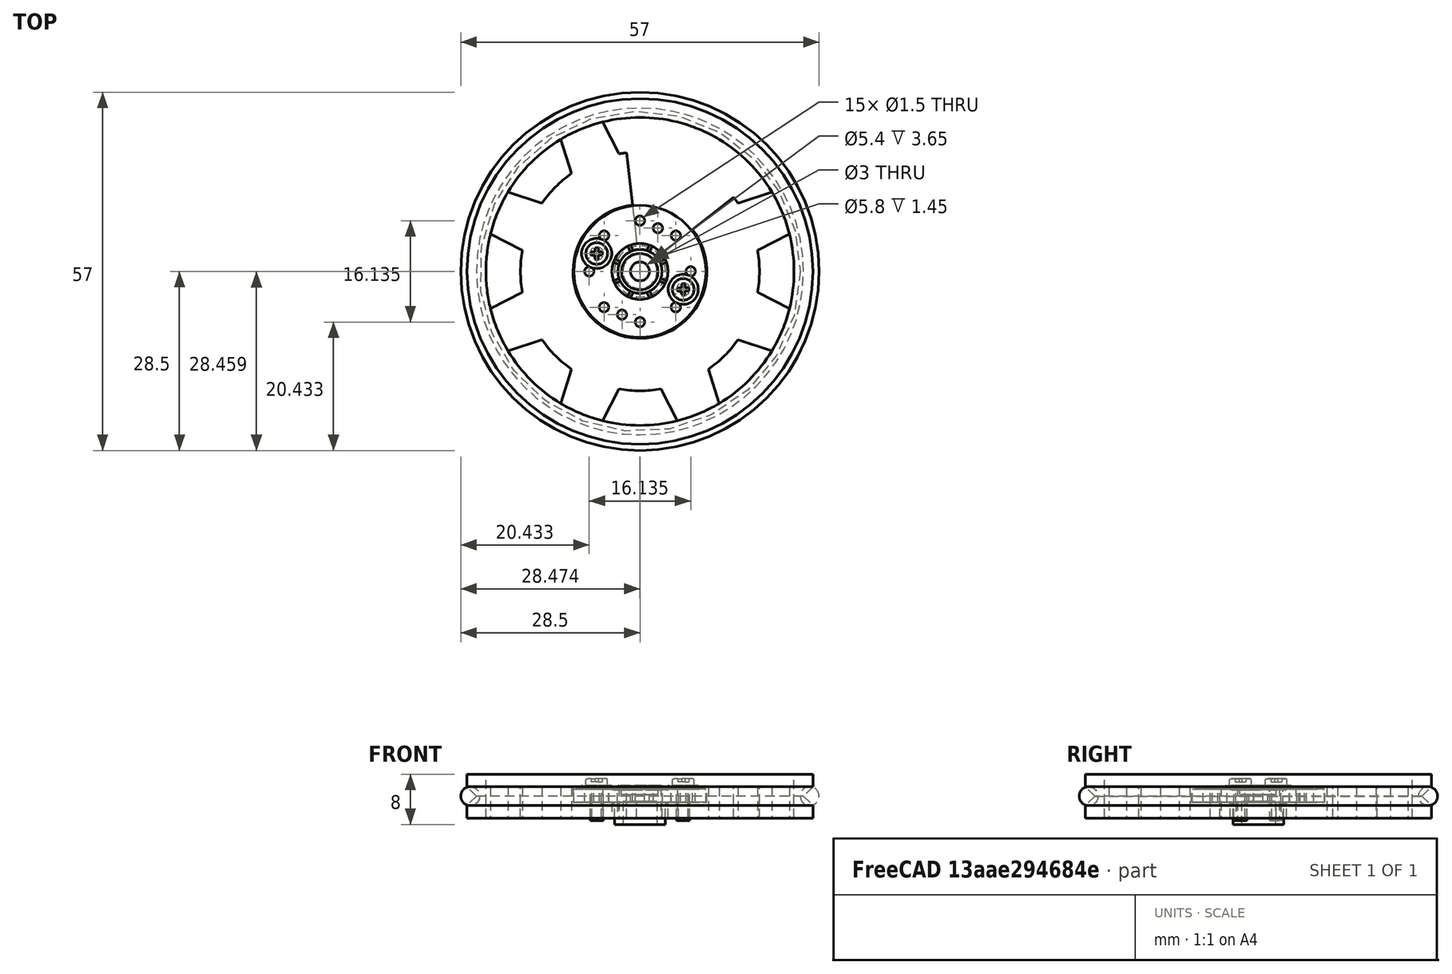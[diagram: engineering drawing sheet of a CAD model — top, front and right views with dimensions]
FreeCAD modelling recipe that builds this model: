
FCSTD DOCUMENT  (FreeCAD 0.14R3702 (Git))
Label: Miniskybot-wheel-open-hardware-logo-futaba3003-assembly
License: CC-BY 3.0
LicenseURL: http://creativecommons.org/licenses/by/3.0/
objects: Part::Feature×4, Part::Torus×1, Part::Compound×1
note: 6 computed .brp shape members not serialized (recipe doc carries the construction recipe); baked Part::Feature solids carry a one-line shape summary decoded from their .brp

FEATURE [Part::Feature] Pocket  label="Miniskybot-wheel-open-hardware-logo-futaba-3003"
  Placement = pos=(0,0,0) rot=(1,0,0;1.5708rad)
  shape: bbox 55 x 55 x 7 mm, 56 faces (baked)
FEATURE [Part::Feature] Fillet  label="servo-rounded-horn"
  Placement = pos=(0,0,-4.5) rot=(0.962637,-0.19148,-0.19148;1.60887rad)
  shape: bbox 21 x 21 x 6.2 mm, 65 faces (baked)
FEATURE [Part::Torus] Torus  label="o-ring"
  Angle1 = -180
  Angle2 = 180
  Angle3 = 360
  Radius1 = 27
  Radius2 = 1.5
FEATURE [Part::Feature] Fillet001  label="bolt-1"
  Placement = pos=(-6.8829,2.85099,1.1) rot=(0,0,1;0rad)
  shape: bbox 4.8 x 4.8 x 6.7 mm, 21 faces (baked)
FEATURE [Part::Feature] Fillet002  label="bolt-2"
  Placement = pos=(6.8829,-2.85099,1.1) rot=(0,0,1;0rad)
  shape: bbox 4.8 x 4.8 x 6.7 mm, 21 faces (baked)
FEATURE [Part::Compound] Compound  label="Miniskybot-wheel-open-hardware-logo-futaba3003-assembly"
  Links = -> [Fillet,Pocket,Torus,Fillet002,Fillet001]
